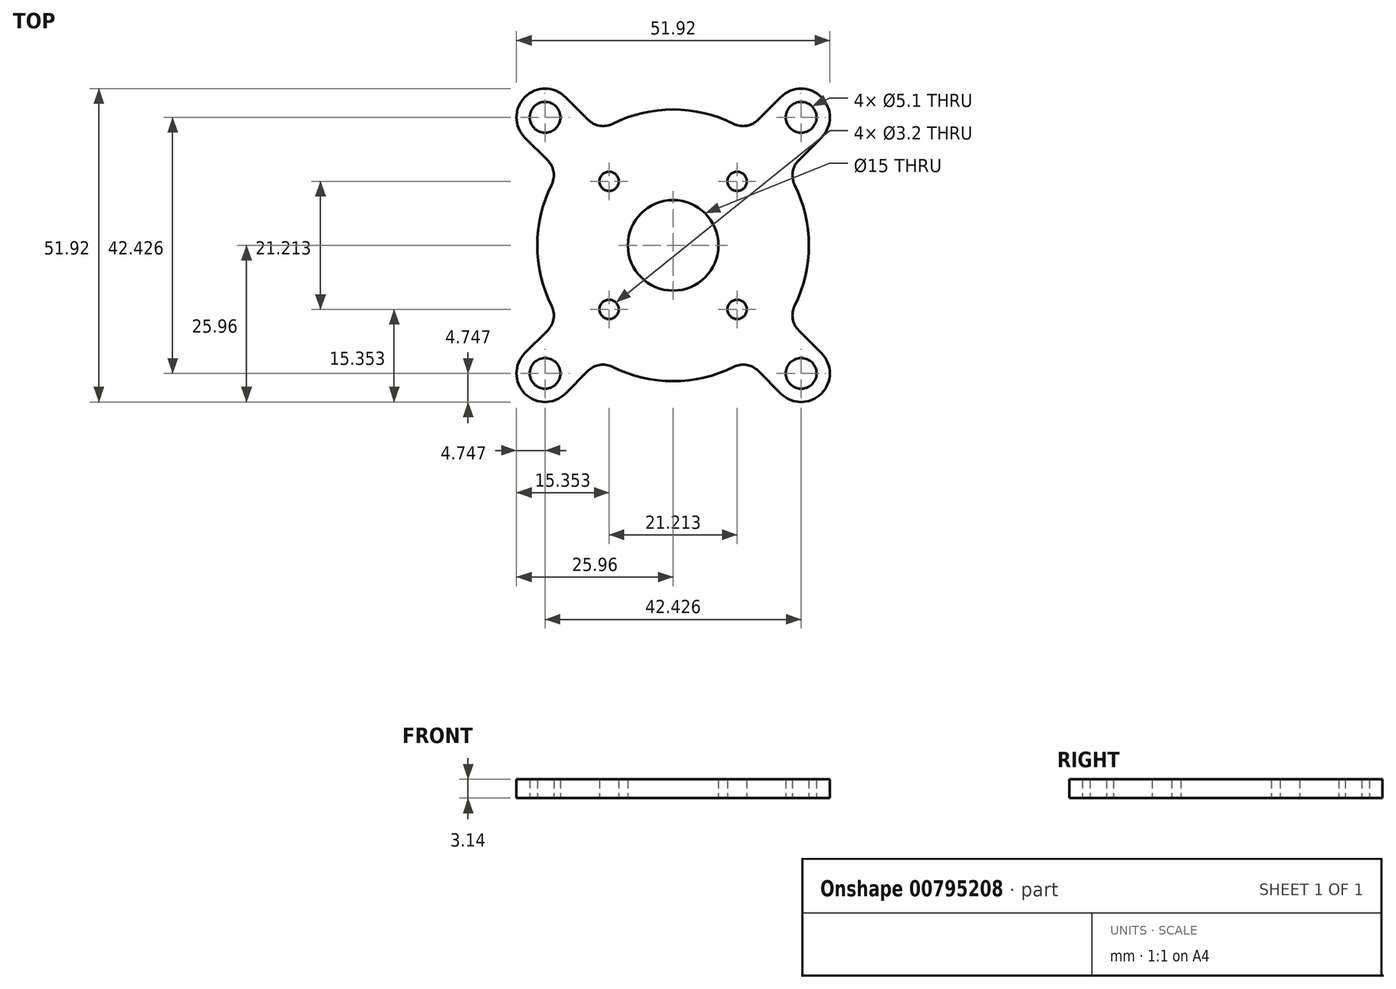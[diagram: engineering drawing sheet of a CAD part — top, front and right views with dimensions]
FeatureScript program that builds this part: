
annotation { "Feature Type Name" : "Feature", "Feature Type Description" : "" }
export const myFeature = defineFeature(function(context is Context, id is Id, definition is map)
    precondition{}
    {
        {
            var Q0;
            Q0=qCreatedBy(makeId("Top.planeOp"),FACE);
            var sketch = newSketch(context, id + "F0", { "sketchPlane" : qUnion([Q0])});
            skCircle(sketch, "E0", {"center": v(0, 0) * mm, "radius": 7.5 * mm});
            skLineSegment(sketch, "E1", {"start": v(-8.84, 8.84) * mm, "end": v(-21.21, 21.21) * mm, "construction": true});
            skCircle(sketch, "E2", {"center": v(0, 0) * mm, "radius": 30 * mm, "construction": true});
            skCircle(sketch, "E3", {"center": v(0, 0) * mm, "radius": 12.5 * mm, "construction": true});
            skArc(sketch, "E4.0.endCap", {"start": v(-24.57, 17.85) * mm, "mid": v(-24.57, 24.57) * mm, "end": v(-17.85, 24.57) * mm});
            skLineSegment(sketch, "E4.0.left", {"start": v(-20.8, 14.08) * mm, "end": v(-24.57, 17.85) * mm});
            skLineSegment(sketch, "E4.0.right", {"start": v(-14.08, 20.8) * mm, "end": v(-17.85, 24.57) * mm});
            skArc(sketch, "E5", {"start": v(-20.14, 10.04) * mm, "mid": v(-22.5, 0) * mm, "end": v(-20.14, -10.04) * mm});
            skCircle(sketch, "E6", {"center": v(-21.21, 21.21) * mm, "radius": 2.55 * mm});
            skCircle(sketch, "E7.1.0", {"center": v(-21.21, -21.21) * mm, "radius": 2.55 * mm});
            skLineSegment(sketch, "E7.1.1", {"start": v(-14.08, -20.8) * mm, "end": v(-17.85, -24.57) * mm});
            skArc(sketch, "E7.1.2", {"start": v(-17.85, -24.57) * mm, "mid": v(-24.57, -24.57) * mm, "end": v(-24.57, -17.85) * mm});
            skLineSegment(sketch, "E7.1.3", {"start": v(-20.8, -14.08) * mm, "end": v(-24.57, -17.85) * mm});
            skCircle(sketch, "E7.2.0", {"center": v(21.21, -21.21) * mm, "radius": 2.55 * mm});
            skLineSegment(sketch, "E7.2.1", {"start": v(20.8, -14.08) * mm, "end": v(24.57, -17.85) * mm});
            skArc(sketch, "E7.2.2", {"start": v(24.57, -17.85) * mm, "mid": v(24.57, -24.57) * mm, "end": v(17.85, -24.57) * mm});
            skLineSegment(sketch, "E7.2.3", {"start": v(14.08, -20.8) * mm, "end": v(17.85, -24.57) * mm});
            skCircle(sketch, "E7.3.0", {"center": v(21.21, 21.21) * mm, "radius": 2.55 * mm});
            skLineSegment(sketch, "E7.3.1", {"start": v(14.08, 20.8) * mm, "end": v(17.85, 24.57) * mm});
            skArc(sketch, "E7.3.2", {"start": v(17.85, 24.57) * mm, "mid": v(24.57, 24.57) * mm, "end": v(24.57, 17.85) * mm});
            skLineSegment(sketch, "E7.3.3", {"start": v(20.8, 14.08) * mm, "end": v(24.57, 17.85) * mm});
            skArc(sketch, "E8.trimOffspring", {"start": v(10.04, 20.14) * mm, "mid": v(0, 22.5) * mm, "end": v(-10.04, 20.14) * mm});
            skArc(sketch, "E9.trimOffspring", {"start": v(20.14, -10.04) * mm, "mid": v(22.5, 0) * mm, "end": v(20.14, 10.04) * mm});
            skArc(sketch, "E10.trimOffspring", {"start": v(-10.04, -20.14) * mm, "mid": v(0, -22.5) * mm, "end": v(10.04, -20.14) * mm});
            skPoint(sketch, "E11.visualSharp", {"position": v(-12.2, 18.91) * mm});
            skArc(sketch, "E11.filletArc", {"start": v(-14.08, 20.8) * mm, "mid": v(-12.16, 19.81) * mm, "end": v(-10.04, 20.14) * mm});
            skPoint(sketch, "E12.visualSharp", {"position": v(12.2, 18.91) * mm});
            skArc(sketch, "E12.filletArc", {"start": v(10.04, 20.14) * mm, "mid": v(12.16, 19.81) * mm, "end": v(14.08, 20.8) * mm});
            skPoint(sketch, "E13.visualSharp", {"position": v(18.91, 12.2) * mm});
            skArc(sketch, "E13.filletArc", {"start": v(20.8, 14.08) * mm, "mid": v(19.81, 12.16) * mm, "end": v(20.14, 10.04) * mm});
            skPoint(sketch, "E14.visualSharp", {"position": v(18.91, -12.2) * mm});
            skArc(sketch, "E14.filletArc", {"start": v(20.14, -10.04) * mm, "mid": v(19.81, -12.16) * mm, "end": v(20.8, -14.08) * mm});
            skPoint(sketch, "E15.visualSharp", {"position": v(12.2, -18.91) * mm});
            skArc(sketch, "E15.filletArc", {"start": v(14.08, -20.8) * mm, "mid": v(12.16, -19.81) * mm, "end": v(10.04, -20.14) * mm});
            skPoint(sketch, "E16.visualSharp", {"position": v(-12.2, -18.91) * mm});
            skArc(sketch, "E16.filletArc", {"start": v(-10.04, -20.14) * mm, "mid": v(-12.16, -19.81) * mm, "end": v(-14.08, -20.8) * mm});
            skPoint(sketch, "E17.visualSharp", {"position": v(-18.91, -12.2) * mm});
            skArc(sketch, "E17.filletArc", {"start": v(-20.8, -14.08) * mm, "mid": v(-19.81, -12.16) * mm, "end": v(-20.14, -10.04) * mm});
            skPoint(sketch, "E18.visualSharp", {"position": v(-18.91, 12.2) * mm});
            skArc(sketch, "E18.filletArc", {"start": v(-20.14, 10.04) * mm, "mid": v(-19.81, 12.16) * mm, "end": v(-20.8, 14.08) * mm});
            skCircle(sketch, "E19", {"center": v(0, 0) * mm, "radius": 15 * mm, "construction": true});
            skCircle(sketch, "E20", {"center": v(-10.6, 10.6) * mm, "radius": 1.6 * mm});
            skCircle(sketch, "E21.1.0", {"center": v(-10.6, -10.6) * mm, "radius": 1.6 * mm});
            skCircle(sketch, "E21.2.0", {"center": v(10.6, -10.6) * mm, "radius": 1.6 * mm});
            skCircle(sketch, "E21.3.0", {"center": v(10.6, 10.6) * mm, "radius": 1.6 * mm});
            skSolve(sketch);
        }
        {
            var Q0;
            Q0 = qSketchRegion(id + "F0", true);
            extrude(context, id + "F1", {"entities" : qUnion([Q0]), "depth" : 3.14 * mm, "offsetDistance" : 25 * mm});
        }
    });
